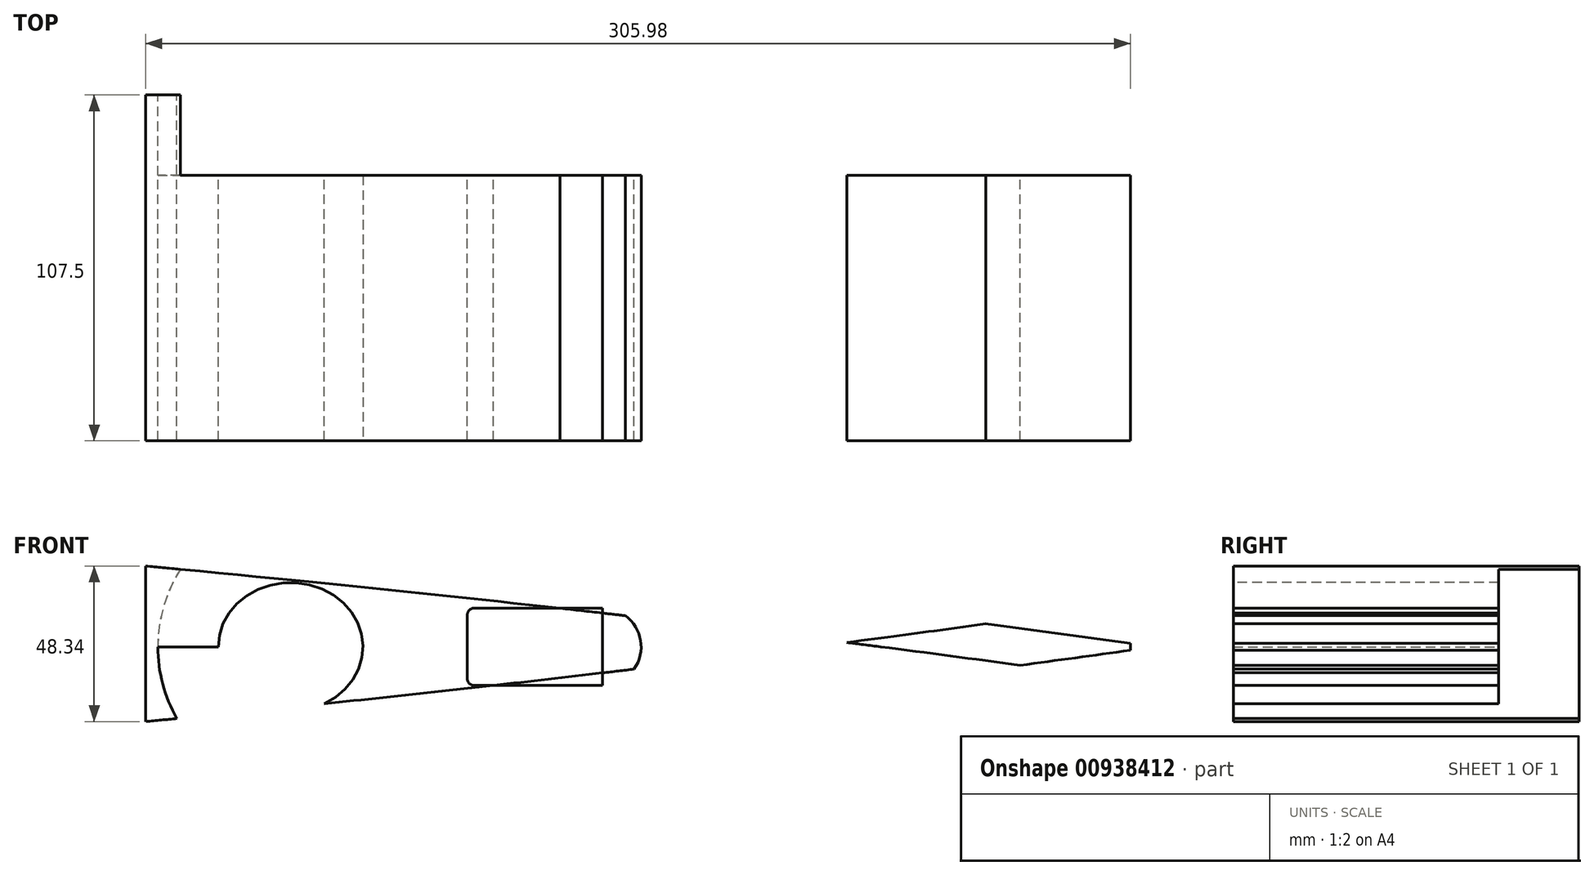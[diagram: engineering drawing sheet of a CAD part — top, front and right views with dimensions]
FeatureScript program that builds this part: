
annotation { "Feature Type Name" : "Feature", "Feature Type Description" : "" }
export const myFeature = defineFeature(function(context is Context, id is Id, definition is map)
    precondition{}
    {
        {
            var Q0;
            Q0=qCreatedBy(makeId("Front.planeOp"),FACE);
            var sketch = newSketch(context, id + "F0", { "sketchPlane" : qUnion([Q0])});
            skLineSegment(sketch, "E0", {"start": v(0, 0) * mm, "end": v(830, 0) * mm});
            skLineSegment(sketch, "E1", {"start": v(23.53, 0) * mm, "end": v(23.53, 22.98) * mm, "construction": true});
            skLineSegment(sketch, "E2", {"start": v(30.64, 0) * mm, "end": v(30.64, 25.86) * mm, "construction": true});
            skLineSegment(sketch, "E3", {"start": v(38.65, 0) * mm, "end": v(38.65, 28.62) * mm, "construction": true});
            skLineSegment(sketch, "E4", {"start": v(47.54, 0) * mm, "end": v(47.54, 31.24) * mm, "construction": true});
            skLineSegment(sketch, "E5", {"start": v(57.28, 0) * mm, "end": v(57.28, 33.72) * mm, "construction": true});
            skLineSegment(sketch, "E6", {"start": v(67.86, 0) * mm, "end": v(67.86, 36.05) * mm, "construction": true});
            skLineSegment(sketch, "E7", {"start": v(79.26, 0) * mm, "end": v(79.26, 38.22) * mm, "construction": true});
            skLineSegment(sketch, "E8", {"start": v(91.44, 0) * mm, "end": v(91.44, 40.22) * mm, "construction": true});
            skLineSegment(sketch, "E9", {"start": v(104.37, 0) * mm, "end": v(104.37, 42.04) * mm, "construction": true});
            skLineSegment(sketch, "E10", {"start": v(118.03, 0) * mm, "end": v(118.03, 43.68) * mm, "construction": true});
            skLineSegment(sketch, "E11", {"start": v(132.38, 0) * mm, "end": v(132.38, 45.13) * mm, "construction": true});
            skLineSegment(sketch, "E12", {"start": v(147.4, 0) * mm, "end": v(147.4, 46.38) * mm, "construction": true});
            skLineSegment(sketch, "E13", {"start": v(163.03, 0) * mm, "end": v(163.03, 47.45) * mm, "construction": true});
            skLineSegment(sketch, "E14", {"start": v(179.25, 0) * mm, "end": v(179.25, 48.31) * mm, "construction": true});
            skLineSegment(sketch, "E15", {"start": v(196.03, 0) * mm, "end": v(196.03, 48.98) * mm, "construction": true});
            skLineSegment(sketch, "E16", {"start": v(213.32, 0) * mm, "end": v(213.32, 49.45) * mm, "construction": true});
            skLineSegment(sketch, "E17", {"start": v(231.08, 0) * mm, "end": v(231.08, 49.73) * mm, "construction": true});
            skLineSegment(sketch, "E18", {"start": v(249.26, 0) * mm, "end": v(249.26, 49.81) * mm, "construction": true});
            skLineSegment(sketch, "E19", {"start": v(267.84, 0) * mm, "end": v(267.84, 49.72) * mm, "construction": true});
            skLineSegment(sketch, "E20", {"start": v(0.48, 0) * mm, "end": v(0.48, 3.54) * mm, "construction": true});
            skLineSegment(sketch, "E21", {"start": v(1.94, 0) * mm, "end": v(1.94, 7) * mm, "construction": true});
            skLineSegment(sketch, "E22", {"start": v(4.35, 0) * mm, "end": v(4.35, 10.38) * mm, "construction": true});
            skLineSegment(sketch, "E23", {"start": v(7.73, 0) * mm, "end": v(7.73, 13.67) * mm, "construction": true});
            skLineSegment(sketch, "E24", {"start": v(12.06, 0) * mm, "end": v(12.06, 16.87) * mm, "construction": true});
            skLineSegment(sketch, "E25", {"start": v(17.33, 0) * mm, "end": v(17.33, 19.98) * mm, "construction": true});
            skLineSegment(sketch, "E26", {"start": v(286.76, 0) * mm, "end": v(286.76, 49.45) * mm, "construction": true});
            skLineSegment(sketch, "E27", {"start": v(305.98, 0) * mm, "end": v(305.98, 49) * mm, "construction": true});
            skLineSegment(sketch, "E28", {"start": v(325.45, 0) * mm, "end": v(325.45, 48.4) * mm, "construction": true});
            skLineSegment(sketch, "E29", {"start": v(345.13, 0) * mm, "end": v(345.13, 47.64) * mm, "construction": true});
            skLineSegment(sketch, "E30", {"start": v(364.98, 0) * mm, "end": v(364.98, 46.75) * mm, "construction": true});
            skLineSegment(sketch, "E31", {"start": v(384.94, 0) * mm, "end": v(384.94, 45.71) * mm, "construction": true});
            skLineSegment(sketch, "E32", {"start": v(404.97, 0) * mm, "end": v(404.97, 44.56) * mm, "construction": true});
            skLineSegment(sketch, "E33", {"start": v(425.03, 0) * mm, "end": v(425.03, 43.3) * mm, "construction": true});
            skLineSegment(sketch, "E34", {"start": v(445.06, 0) * mm, "end": v(445.06, 41.93) * mm, "construction": true});
            skLineSegment(sketch, "E35", {"start": v(465.02, 0) * mm, "end": v(465.02, 40.47) * mm, "construction": true});
            skLineSegment(sketch, "E36", {"start": v(484.87, 0) * mm, "end": v(484.87, 38.94) * mm, "construction": true});
            skLineSegment(sketch, "E37", {"start": v(504.55, 0) * mm, "end": v(504.55, 37.33) * mm, "construction": true});
            skLineSegment(sketch, "E38", {"start": v(524.02, 0) * mm, "end": v(524.02, 35.67) * mm, "construction": true});
            skLineSegment(sketch, "E39", {"start": v(543.24, 0) * mm, "end": v(543.24, 33.96) * mm, "construction": true});
            skLineSegment(sketch, "E40", {"start": v(562.16, 0) * mm, "end": v(562.16, 32.21) * mm, "construction": true});
            skLineSegment(sketch, "E41", {"start": v(580.74, 0) * mm, "end": v(580.74, 30.44) * mm, "construction": true});
            skLineSegment(sketch, "E42", {"start": v(598.92, 0) * mm, "end": v(598.92, 28.64) * mm, "construction": true});
            skLineSegment(sketch, "E43", {"start": v(633.97, 0) * mm, "end": v(633.97, 25.03) * mm, "construction": true});
            skLineSegment(sketch, "E44", {"start": v(616.68, 0) * mm, "end": v(616.68, 26.83) * mm, "construction": true});
            skLineSegment(sketch, "E45", {"start": v(650.75, 0) * mm, "end": v(650.75, 23.23) * mm, "construction": true});
            skLineSegment(sketch, "E46", {"start": v(666.97, 0) * mm, "end": v(666.97, 21.44) * mm, "construction": true});
            skLineSegment(sketch, "E47", {"start": v(682.6, 0) * mm, "end": v(682.6, 19.68) * mm, "construction": true});
            skLineSegment(sketch, "E48", {"start": v(697.62, 0) * mm, "end": v(697.62, 17.96) * mm, "construction": true});
            skLineSegment(sketch, "E49", {"start": v(711.97, 0) * mm, "end": v(711.97, 16.27) * mm, "construction": true});
            skLineSegment(sketch, "E50", {"start": v(725.63, 0) * mm, "end": v(725.63, 14.64) * mm, "construction": true});
            skLineSegment(sketch, "E51", {"start": v(738.56, 0) * mm, "end": v(738.56, 13.06) * mm, "construction": true});
            skLineSegment(sketch, "E52", {"start": v(750.74, 0) * mm, "end": v(750.74, 11.55) * mm, "construction": true});
            skLineSegment(sketch, "E53", {"start": v(762.14, 0) * mm, "end": v(762.14, 10.11) * mm, "construction": true});
            skLineSegment(sketch, "E54", {"start": v(791.35, 0) * mm, "end": v(791.35, 6.32) * mm, "construction": true});
            skLineSegment(sketch, "E55", {"start": v(799.36, 0) * mm, "end": v(799.36, 5.25) * mm, "construction": true});
            skLineSegment(sketch, "E56", {"start": v(806.47, 0) * mm, "end": v(806.47, 4.29) * mm, "construction": true});
            skLineSegment(sketch, "E57", {"start": v(782.46, 0) * mm, "end": v(782.46, 7.49) * mm, "construction": true});
            skLineSegment(sketch, "E58", {"start": v(812.67, 0) * mm, "end": v(812.67, 3.45) * mm, "construction": true});
            skLineSegment(sketch, "E59", {"start": v(817.94, 0) * mm, "end": v(817.94, 2.72) * mm, "construction": true});
            skLineSegment(sketch, "E60", {"start": v(822.27, 0) * mm, "end": v(822.27, 2.12) * mm, "construction": true});
            skLineSegment(sketch, "E61", {"start": v(825.65, 0) * mm, "end": v(825.65, 1.65) * mm, "construction": true});
            skLineSegment(sketch, "E62", {"start": v(828.06, 0) * mm, "end": v(828.06, 1.32) * mm, "construction": true});
            skLineSegment(sketch, "E63", {"start": v(772.72, 0) * mm, "end": v(772.72, 8.76) * mm, "construction": true});
            skLineSegment(sketch, "E64", {"start": v(829.52, 0) * mm, "end": v(829.52, 1.11) * mm, "construction": true});
            skLineSegment(sketch, "E65", {"start": v(830, 0) * mm, "end": v(830, 1.05) * mm});
            skFitSpline(sketch, "E66", {"points": [v(0, 0) * mm, v(0.48, 3.54) * mm, v(1.94, 7) * mm, v(4.35, 10.38) * mm, v(7.73, 13.67) * mm, v(12.06, 16.87) * mm, v(17.33, 19.98) * mm, v(23.53, 22.98) * mm, v(30.64, 25.86) * mm, v(38.65, 28.62) * mm, v(47.54, 31.24) * mm, v(57.28, 33.72) * mm, v(67.86, 36.05) * mm, v(79.26, 38.22) * mm, v(91.44, 40.22) * mm, v(104.37, 42.04) * mm, v(118.03, 43.68) * mm, v(132.38, 45.13) * mm, v(147.4, 46.39) * mm, v(163.03, 47.45) * mm, v(179.25, 48.31) * mm, v(196.03, 48.98) * mm, v(213.32, 49.45) * mm, v(231.08, 49.73) * mm, v(249.26, 49.81) * mm, v(267.84, 49.72) * mm, v(286.76, 49.45) * mm, v(305.98, 49) * mm, v(325.45, 48.4) * mm, v(345.13, 47.64) * mm, v(364.98, 46.75) * mm, v(384.94, 45.71) * mm, v(404.97, 44.56) * mm, v(425.03, 43.3) * mm, v(445.06, 41.93) * mm, v(465.02, 40.47) * mm, v(484.87, 38.94) * mm, v(504.55, 37.33) * mm, v(524.02, 35.67) * mm, v(543.24, 33.96) * mm, v(562.16, 32.21) * mm, v(580.74, 30.44) * mm, v(598.92, 28.64) * mm, v(616.68, 26.83) * mm, v(633.97, 25.03) * mm, v(650.75, 23.23) * mm, v(666.97, 21.44) * mm, v(682.6, 19.68) * mm, v(697.62, 17.96) * mm, v(711.97, 16.27) * mm, v(725.63, 14.64) * mm, v(738.56, 13.06) * mm, v(750.74, 11.55) * mm, v(762.14, 10.11) * mm, v(772.72, 8.76) * mm, v(782.46, 7.49) * mm, v(791.35, 6.32) * mm, v(799.36, 5.25) * mm, v(806.47, 4.29) * mm, v(812.67, 3.45) * mm, v(817.94, 2.72) * mm, v(822.27, 2.12) * mm, v(825.65, 1.65) * mm, v(828.06, 1.32) * mm, v(829.52, 1.11) * mm, v(830, 1.05) * mm], "startDerivative": vector(34.1, 427.03) * mm, "endDerivative": vector(137.1, -19.25) * mm});
            skFitSpline(sketch, "E67.MirrorCS", {"points": [v(0, 0) * mm, v(0.48, -3.54) * mm, v(1.94, -7) * mm, v(4.35, -10.38) * mm, v(7.73, -13.67) * mm, v(12.06, -16.87) * mm, v(17.33, -19.98) * mm, v(23.53, -22.98) * mm, v(30.64, -25.86) * mm, v(38.65, -28.62) * mm, v(47.54, -31.24) * mm, v(57.28, -33.72) * mm, v(67.86, -36.05) * mm, v(79.26, -38.22) * mm, v(91.44, -40.22) * mm, v(104.37, -42.04) * mm, v(118.03, -43.68) * mm, v(132.38, -45.13) * mm, v(147.4, -46.39) * mm, v(163.03, -47.45) * mm, v(179.25, -48.31) * mm, v(196.03, -48.98) * mm, v(213.32, -49.45) * mm, v(231.08, -49.73) * mm, v(249.26, -49.81) * mm, v(267.84, -49.72) * mm, v(286.76, -49.45) * mm, v(305.98, -49) * mm, v(325.45, -48.4) * mm, v(345.13, -47.64) * mm, v(364.98, -46.75) * mm, v(384.94, -45.71) * mm, v(404.97, -44.56) * mm, v(425.03, -43.3) * mm, v(445.06, -41.93) * mm, v(465.02, -40.47) * mm, v(484.87, -38.94) * mm, v(504.55, -37.33) * mm, v(524.02, -35.67) * mm, v(543.24, -33.96) * mm, v(562.16, -32.21) * mm, v(580.74, -30.44) * mm, v(598.92, -28.64) * mm, v(616.68, -26.83) * mm, v(633.97, -25.03) * mm, v(650.75, -23.23) * mm, v(666.97, -21.44) * mm, v(682.6, -19.68) * mm, v(697.62, -17.96) * mm, v(711.97, -16.27) * mm, v(725.63, -14.64) * mm, v(738.56, -13.06) * mm, v(750.74, -11.55) * mm, v(762.14, -10.11) * mm, v(772.72, -8.76) * mm, v(782.46, -7.49) * mm, v(791.35, -6.32) * mm, v(799.36, -5.25) * mm, v(806.47, -4.29) * mm, v(812.67, -3.45) * mm, v(817.94, -2.72) * mm, v(822.27, -2.12) * mm, v(825.65, -1.65) * mm, v(828.06, -1.32) * mm, v(829.52, -1.11) * mm, v(830, -1.05) * mm], "startDerivative": vector(34.1, -427.03) * mm, "endDerivative": vector(137.1, 19.25) * mm});
            skLineSegment(sketch, "E68.MirrorCS", {"start": v(830, 0) * mm, "end": v(830, -1.05) * mm});
            skLineSegment(sketch, "E69", {"start": v(163.03, 47.45) * mm, "end": v(163.03, -47.45) * mm});
            skLineSegment(sketch, "E70", {"start": v(204.25, -49.23) * mm, "end": v(204.25, -33.23) * mm});
            skLineSegment(sketch, "E71", {"start": v(204.25, -33.23) * mm, "end": v(179.25, -33.23) * mm});
            skLineSegment(sketch, "E72", {"start": v(179.25, -33.23) * mm, "end": v(179.25, 33.23) * mm});
            skLineSegment(sketch, "E73", {"start": v(179.25, 33.23) * mm, "end": v(204.25, 33.23) * mm});
            skLineSegment(sketch, "E74", {"start": v(204.25, 33.23) * mm, "end": v(204.25, 49.23) * mm});
            skLineSegment(sketch, "E75", {"start": v(524.02, 35.67) * mm, "end": v(524.02, -35.67) * mm});
            skLineSegment(sketch, "E76", {"start": v(479.55, -39.36) * mm, "end": v(479.55, -23.36) * mm});
            skLineSegment(sketch, "E77", {"start": v(479.55, -23.36) * mm, "end": v(504.55, -23.36) * mm});
            skLineSegment(sketch, "E78", {"start": v(504.55, -23.36) * mm, "end": v(504.55, 23.36) * mm});
            skLineSegment(sketch, "E79", {"start": v(504.55, 23.36) * mm, "end": v(479.55, 23.36) * mm});
            skLineSegment(sketch, "E80", {"start": v(479.55, 23.36) * mm, "end": v(479.55, 39.36) * mm});
            skEllipse(sketch, "E81", {"center": v(240.25, 0) * mm, "majorRadius": 36.5 * mm, "minorRadius": 30 * mm, "majorAxis": v(1, 0)});
            skEllipse(sketch, "E82.1.0.0", {"center": v(333.25, 0) * mm, "majorRadius": 36.5 * mm, "minorRadius": 30 * mm, "majorAxis": v(1, 0)});
            skLineSegment(sketch, "E82.direction1", {"start": v(240.25, 0) * mm, "end": v(333.25, 0) * mm, "construction": true});
            skEllipse(sketch, "E83", {"center": v(425.03, 0) * mm, "majorRadius": 28 * mm, "minorRadius": 36.5 * mm, "majorAxis": v(0, -1)});
            skFitSpline(sketch, "E84.0", {"points": [v(19.9, 0) * mm, v(19.93, 0.28) * mm, v(19.97, 0.77) * mm, v(20.03, 1.33) * mm, v(20.07, 1.63) * mm, v(20.1, 1.78) * mm, v(20.12, 1.85) * mm, v(20.12, 1.88) * mm, v(20.13, 1.92) * mm, v(20.16, 1.99) * mm, v(20.2, 2.1) * mm, v(20.28, 2.3) * mm, v(20.43, 2.58) * mm, v(20.63, 2.94) * mm, v(20.87, 3.32) * mm, v(21.13, 3.7) * mm, v(21.53, 4.23) * mm, v(22.12, 4.91) * mm, v(22.98, 5.8) * mm, v(24.01, 6.71) * mm, v(25.19, 7.65) * mm, v(26.5, 8.6) * mm, v(28.4, 9.86) * mm, v(31.06, 11.42) * mm, v(34.64, 13.25) * mm, v(38.55, 15) * mm, v(44.15, 17.24) * mm, v(51.77, 19.86) * mm, v(61.74, 22.7) * mm, v(72.4, 25.26) * mm, v(83.62, 27.56) * mm, v(95.37, 29.62) * mm, v(107.56, 31.45) * mm, v(124.36, 33.6) * mm, v(146.26, 35.8) * mm, v(173.73, 37.69) * mm, v(202.17, 38.91) * mm, v(231.43, 39.53) * mm, v(261.35, 39.6) * mm, v(291.8, 39.18) * mm, v(322.69, 38.31) * mm, v(364.28, 36.62) * mm, v(416.8, 33.63) * mm, v(479.93, 28.95) * mm, v(531.98, 24.38) * mm, v(572.9, 20.44) * mm, v(603.14, 17.37) * mm, v(632.79, 14.2) * mm, v(661.73, 10.99) * mm, v(689.84, 7.73) * mm, v(716.93, 4.47) * mm, v(738.52, 1.78) * mm, v(755.07, -0.33) * mm, v(767.08, -1.9) * mm, v(778.65, -3.43) * mm, v(789.72, -4.91) * mm, v(800.24, -6.35) * mm, v(810.11, -7.7) * mm, v(817.7, -8.77) * mm, v(823.32, -9.57) * mm, v(826.6, -10.03) * mm, v(829.07, -10.39) * mm, v(830.84, -10.64) * mm, v(832.51, -10.88) * mm, v(834.08, -11.1) * mm, v(835.26, -11.27) * mm, v(836.14, -11.4) * mm, v(836.78, -11.5) * mm, v(837.37, -11.58) * mm, v(837.78, -11.64) * mm, v(838.05, -11.68) * mm, v(838.28, -11.71) * mm, v(838.4, -11.73) * mm, v(838.5, -11.74) * mm]});
            skFitSpline(sketch, "E85.MirrorCS", {"points": [v(19.9, 0) * mm, v(19.93, -0.28) * mm, v(19.97, -0.77) * mm, v(20.03, -1.33) * mm, v(20.08, -1.63) * mm, v(20.1, -1.78) * mm, v(20.12, -1.85) * mm, v(20.13, -1.87) * mm, v(20.14, -1.92) * mm, v(20.16, -1.99) * mm, v(20.2, -2.1) * mm, v(20.29, -2.29) * mm, v(20.44, -2.58) * mm, v(20.64, -2.94) * mm, v(20.88, -3.31) * mm, v(21.15, -3.7) * mm, v(21.55, -4.22) * mm, v(22.13, -4.9) * mm, v(23, -5.78) * mm, v(24.04, -6.7) * mm, v(25.22, -7.63) * mm, v(26.52, -8.57) * mm, v(28.44, -9.83) * mm, v(31.1, -11.38) * mm, v(34.7, -13.2) * mm, v(38.6, -14.93) * mm, v(44.21, -17.15) * mm, v(51.85, -19.74) * mm, v(61.83, -22.54) * mm, v(72.49, -25.06) * mm, v(83.73, -27.32) * mm, v(95.48, -29.34) * mm, v(107.68, -31.12) * mm, v(124.49, -33.22) * mm, v(146.4, -35.32) * mm, v(173.87, -37.11) * mm, v(202.32, -38.23) * mm, v(231.57, -38.74) * mm, v(261.5, -38.7) * mm, v(291.95, -38.16) * mm, v(322.83, -37.18) * mm, v(364.42, -35.33) * mm, v(416.93, -32.14) * mm, v(480.03, -27.22) * mm, v(532.07, -22.46) * mm, v(572.98, -18.36) * mm, v(603.2, -15.18) * mm, v(632.84, -11.91) * mm, v(661.77, -8.58) * mm, v(689.86, -5.22) * mm, v(716.95, -1.86) * mm, v(738.52, 0.91) * mm, v(755.06, 3.1) * mm, v(767.06, 4.7) * mm, v(778.63, 6.27) * mm, v(789.7, 7.8) * mm, v(800.21, 9.27) * mm, v(810.08, 10.67) * mm, v(817.67, 11.77) * mm, v(823.28, 12.58) * mm, v(826.56, 13.06) * mm, v(829.03, 13.42) * mm, v(830.8, 13.68) * mm, v(832.47, 13.93) * mm, v(834.03, 14.16) * mm, v(835.21, 14.33) * mm, v(836.1, 14.46) * mm, v(836.73, 14.56) * mm, v(837.32, 14.64) * mm, v(837.73, 14.7) * mm, v(838, 14.75) * mm, v(838.23, 14.78) * mm, v(838.36, 14.8) * mm, v(838.45, 14.81) * mm]});
            skLineSegment(sketch, "E86", {"start": v(100.03, 30.3) * mm, "end": v(134.03, 30.3) * mm});
            skLineSegment(sketch, "E87", {"start": v(140.03, 24.3) * mm, "end": v(140.03, -24.26) * mm});
            skLineSegment(sketch, "E88", {"start": v(133.98, -30.26) * mm, "end": v(100.03, -29.99) * mm});
            skPoint(sketch, "E89.visualSharp", {"position": v(140.03, 30.3) * mm});
            skArc(sketch, "E89.filletArc", {"start": v(140.03, 24.3) * mm, "mid": v(138.27, 28.55) * mm, "end": v(134.03, 30.3) * mm});
            skPoint(sketch, "E90.visualSharp", {"position": v(140.03, -30.3) * mm});
            skArc(sketch, "E90.filletArc", {"start": v(133.98, -30.26) * mm, "mid": v(138.25, -28.52) * mm, "end": v(140.03, -24.26) * mm});
            skEllipse(sketch, "E91", {"center": v(569.02, 0) * mm, "majorRadius": 20 * mm, "minorRadius": 22.5 * mm, "majorAxis": v(0, -1)});
            skLineSegment(sketch, "E92.bottom", {"start": v(625.97, -12) * mm, "end": v(665.97, -12) * mm});
            skLineSegment(sketch, "E92.top", {"start": v(625.97, 12) * mm, "end": v(665.97, 12) * mm});
            skLineSegment(sketch, "E92.left", {"start": v(623.97, -10) * mm, "end": v(623.97, 10) * mm});
            skLineSegment(sketch, "E92.right", {"start": v(665.97, -12) * mm, "end": v(665.97, 12) * mm});
            skPoint(sketch, "E92.middle", {"position": v(644.97, 0) * mm});
            skArc(sketch, "E93", {"start": v(665.97, 12) * mm, "mid": v(677.97, 0) * mm, "end": v(665.97, -12) * mm});
            skPoint(sketch, "E94.visualSharp", {"position": v(623.97, 12) * mm});
            skArc(sketch, "E94.filletArc", {"start": v(625.97, 12) * mm, "mid": v(624.56, 11.41) * mm, "end": v(623.97, 10) * mm});
            skPoint(sketch, "E95.visualSharp", {"position": v(623.97, -12) * mm});
            skArc(sketch, "E95.filletArc", {"start": v(623.97, -10) * mm, "mid": v(624.56, -11.41) * mm, "end": v(625.97, -12) * mm});
            skPoint(sketch, "E96", {"position": v(276.75, 0) * mm});
            skPoint(sketch, "E97", {"position": v(296.75, 0) * mm});
            skLineSegment(sketch, "E98.bottom", {"start": v(276.26, 65.67) * mm, "end": v(297.26, 65.67) * mm});
            skLineSegment(sketch, "E98.top", {"start": v(276.26, 33.23) * mm, "end": v(297.26, 33.23) * mm});
            skLineSegment(sketch, "E98.left", {"start": v(276.26, 65.67) * mm, "end": v(276.26, 33.23) * mm});
            skLineSegment(sketch, "E98.right", {"start": v(297.26, 65.67) * mm, "end": v(297.26, 33.23) * mm});
            skPoint(sketch, "E99", {"position": v(369.75, 0) * mm});
            skPoint(sketch, "E100", {"position": v(388.53, 0) * mm});
            skLineSegment(sketch, "E101", {"start": v(379.14, 0) * mm, "end": v(379.14, 46.03) * mm, "construction": true});
            skLineSegment(sketch, "E102.bottom", {"start": v(368.64, 58.81) * mm, "end": v(389.64, 58.81) * mm});
            skLineSegment(sketch, "E102.top", {"start": v(368.64, 33.23) * mm, "end": v(389.64, 33.23) * mm});
            skLineSegment(sketch, "E102.left", {"start": v(368.64, 58.81) * mm, "end": v(368.64, 33.23) * mm});
            skLineSegment(sketch, "E102.right", {"start": v(389.64, 58.81) * mm, "end": v(389.64, 33.23) * mm});
            skLineSegment(sketch, "E103.MirrorCS", {"start": v(297.26, -65.67) * mm, "end": v(297.26, -33.23) * mm});
            skLineSegment(sketch, "E104.MirrorCS", {"start": v(276.26, -65.67) * mm, "end": v(297.26, -65.67) * mm});
            skLineSegment(sketch, "E105.MirrorCS", {"start": v(276.26, -65.67) * mm, "end": v(276.26, -33.23) * mm});
            skLineSegment(sketch, "E106.MirrorCS", {"start": v(276.26, -33.23) * mm, "end": v(297.26, -33.23) * mm});
            skLineSegment(sketch, "E107.MirrorCS", {"start": v(368.64, -58.81) * mm, "end": v(389.64, -58.81) * mm});
            skLineSegment(sketch, "E108.MirrorCS", {"start": v(368.64, -58.81) * mm, "end": v(368.64, -33.23) * mm});
            skLineSegment(sketch, "E109.MirrorCS", {"start": v(389.64, -58.81) * mm, "end": v(389.64, -33.23) * mm});
            skLineSegment(sketch, "E110.MirrorCS", {"start": v(368.64, -33.23) * mm, "end": v(389.64, -33.23) * mm});
            skArc(sketch, "E111", {"start": v(543.24, 33.96) * mm, "mid": v(527.77, 0) * mm, "end": v(543.24, -33.96) * mm});
            skSolve(sketch);
        }
        {
            var Q0;
            {var subQ13=sQuery(id+"F0.wireOp",EDGE,"E65");Q0=makeQuery(id+"F0.imprint","IMPRINT",FACE,{"disambiguationData":[TD([[makeQuery(id+"F0.imprint","IMPRINT",EDGE,{"derivedFrom":subQ13}),1.0]])]});}
            var Q1;
            {var subQ0=sQuery(id+"F0.wireOp",EDGE,"E75");var subQ1=sQuery(id+"F0.wireOp",EDGE,"E0");var subQ2=makeQuery(id+"F0.imprint","INTERSECT",VERTEX,{"derivedFrom":[subQ1,subQ0]});Q1=makeQuery(id+"F0.imprint","IMPRINT",FACE,{"disambiguationData":[TD([[makeQuery(id+"F0.imprint","IMPRINT",EDGE,{"disambiguationData":[TD([[subQ2,-1.0]])],"derivedFrom":subQ1}),1.0]])]});}
            var Q2;
            {var subQ0=sQuery(id+"F0.wireOp",EDGE,"E75");var subQ1=sQuery(id+"F0.wireOp",EDGE,"E0");var subQ2=makeQuery(id+"F0.imprint","INTERSECT",VERTEX,{"derivedFrom":[subQ1,subQ0]});Q2=makeQuery(id+"F0.imprint","IMPRINT",FACE,{"disambiguationData":[TD([[makeQuery(id+"F0.imprint","IMPRINT",EDGE,{"disambiguationData":[TD([[subQ2,-1.0]])],"derivedFrom":subQ1}),-1.0]])]});}
            var Q3;
            {var subQ11=sQuery(id+"F0.wireOp",EDGE,"E68.MirrorCS");Q3=makeQuery(id+"F0.imprint","IMPRINT",FACE,{"disambiguationData":[TD([[makeQuery(id+"F0.imprint","IMPRINT",EDGE,{"derivedFrom":subQ11}),-1.0]])]});}
            var Q4;
            {var subQ0=sQuery(id+"F0.wireOp",EDGE,"E91");var subQ1=sQuery(id+"F0.wireOp",EDGE,"E0");var subQ2=makeQuery(id+"F0.imprint","INTERSECT",VERTEX,{"disambiguationData":[OD(0.0)],"derivedFrom":[subQ1,subQ0]});Q4=makeQuery(id+"F0.imprint","IMPRINT",FACE,{"disambiguationData":[TD([[makeQuery(id+"F0.imprint","IMPRINT",EDGE,{"disambiguationData":[TD([[subQ2,-1.0]])],"derivedFrom":subQ1}),-1.0]])]});}
            var Q5;
            {var subQ0=sQuery(id+"F0.wireOp",EDGE,"E91");var subQ1=sQuery(id+"F0.wireOp",EDGE,"E0");var subQ2=makeQuery(id+"F0.imprint","INTERSECT",VERTEX,{"disambiguationData":[OD(0.0)],"derivedFrom":[subQ1,subQ0]});Q5=makeQuery(id+"F0.imprint","IMPRINT",FACE,{"disambiguationData":[TD([[makeQuery(id+"F0.imprint","IMPRINT",EDGE,{"disambiguationData":[TD([[subQ2,-1.0]])],"derivedFrom":subQ1}),1.0]])]});}
            var Q6;
            {var subQ1=sQuery(id+"F0.wireOp",EDGE,"E92.bottom");Q6=makeQuery(id+"F0.imprint","IMPRINT",FACE,{"disambiguationData":[TD([[makeQuery(id+"F0.imprint","IMPRINT",EDGE,{"derivedFrom":subQ1}),1.0]])]});}
            var Q7;
            {var subQ1=sQuery(id+"F0.wireOp",EDGE,"E92.top");Q7=makeQuery(id+"F0.imprint","IMPRINT",FACE,{"disambiguationData":[TD([[makeQuery(id+"F0.imprint","IMPRINT",EDGE,{"derivedFrom":subQ1}),-1.0]])]});}
            var Q8;
            {var subQ0=sQuery(id+"F0.wireOp",EDGE,"E92.right");var subQ1=sQuery(id+"F0.wireOp",EDGE,"E0");var subQ2=makeQuery(id+"F0.imprint","INTERSECT",VERTEX,{"derivedFrom":[subQ1,subQ0]});Q8=makeQuery(id+"F0.imprint","IMPRINT",FACE,{"disambiguationData":[TD([[makeQuery(id+"F0.imprint","IMPRINT",EDGE,{"disambiguationData":[TD([[subQ2,-1.0]])],"derivedFrom":subQ1}),-1.0]])]});}
            var Q9;
            {var subQ0=sQuery(id+"F0.wireOp",EDGE,"E92.right");var subQ1=sQuery(id+"F0.wireOp",EDGE,"E0");var subQ2=makeQuery(id+"F0.imprint","INTERSECT",VERTEX,{"derivedFrom":[subQ1,subQ0]});Q9=makeQuery(id+"F0.imprint","IMPRINT",FACE,{"disambiguationData":[TD([[makeQuery(id+"F0.imprint","IMPRINT",EDGE,{"disambiguationData":[TD([[subQ2,-1.0]])],"derivedFrom":subQ1}),1.0]])]});}
            extrude(context, id + "F1", {"entities" : qUnion([Q0, Q1, Q2, Q3, Q4, Q5, Q6, Q7, Q8, Q9]), "depth" : 82.5 * mm, "offsetDistance" : 25 * mm});
        }
        {
            var Q0;
            {var subQ0=sQuery(id+"F0.wireOp",EDGE,"E75");var subQ1=sQuery(id+"F0.wireOp",EDGE,"E0");var subQ2=makeQuery(id+"F0.imprint","INTERSECT",VERTEX,{"derivedFrom":[subQ1,subQ0]});Q0=makeQuery(id+"F0.imprint","IMPRINT",FACE,{"disambiguationData":[TD([[makeQuery(id+"F0.imprint","IMPRINT",EDGE,{"disambiguationData":[TD([[subQ2,-1.0]])],"derivedFrom":subQ1}),1.0]])]});}
            var Q1;
            {var subQ0=sQuery(id+"F0.wireOp",EDGE,"E75");var subQ1=sQuery(id+"F0.wireOp",EDGE,"E0");var subQ2=makeQuery(id+"F0.imprint","INTERSECT",VERTEX,{"derivedFrom":[subQ1,subQ0]});Q1=makeQuery(id+"F0.imprint","IMPRINT",FACE,{"disambiguationData":[TD([[makeQuery(id+"F0.imprint","IMPRINT",EDGE,{"disambiguationData":[TD([[subQ2,-1.0]])],"derivedFrom":subQ1}),-1.0]])]});}
            extrude(context, id + "F2", {"entities" : qUnion([Q0, Q1]), "operationType" : NewBodyOperationType.ADD, "oppositeDirection" : true, "depth" : 25 * mm, "offsetDistance" : 25 * mm});
        }
        {
            var Q0;
            {var subQ13=sQuery(id+"F0.wireOp",EDGE,"E65");Q0=makeQuery(id+"F0.imprint","IMPRINT",FACE,{"disambiguationData":[TD([[makeQuery(id+"F0.imprint","IMPRINT",EDGE,{"derivedFrom":subQ13}),1.0]])]});}
            var sketch = newSketch(context, id + "F3", { "sketchPlane" : qUnion([Q0])});
            skCircle(sketch, "E112", {"center": v(572.77, 0) * mm, "radius": 12.5 * mm});
            skSolve(sketch);
        }
        {
            var Q0;
            Q0=makeQuery(id+"F3.imprint","IMPRINT",FACE,{"disambiguationData":[TD([[makeQuery(id+"F3.imprint","IMPRINT",EDGE,{"derivedFrom":sQuery(id+"F3.wireOp",EDGE,"E112")}),1.0]])]});
            extrude(context, id + "F4", {"entities" : qUnion([Q0]), "operationType" : NewBodyOperationType.REMOVE, "depth" : 60 * mm, "offsetDistance" : 25 * mm});
        }
    });
